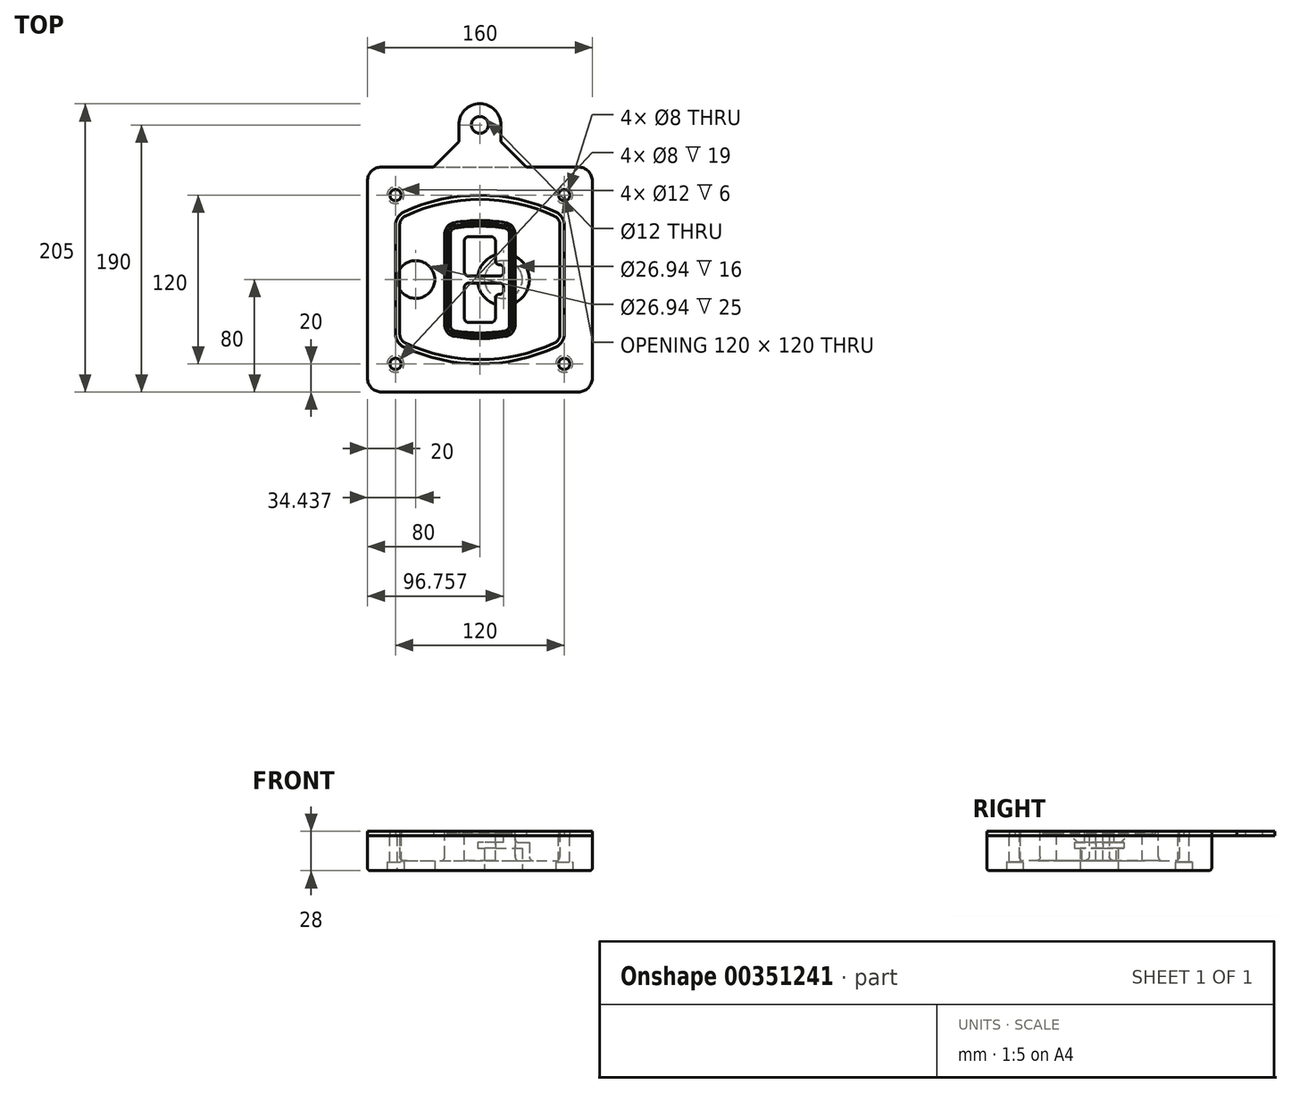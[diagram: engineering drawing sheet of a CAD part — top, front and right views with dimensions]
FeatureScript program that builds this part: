
annotation { "Feature Type Name" : "Feature", "Feature Type Description" : "" }
export const myFeature = defineFeature(function(context is Context, id is Id, definition is map)
    precondition{}
    {
        {
            var Q0;
            Q0=qCreatedBy(makeId("Top.planeOp"),FACE);
            var sketch = newSketch(context, id + "F0", { "sketchPlane" : qUnion([Q0])});
            skPoint(sketch, "E0.rect.middle", {"position": v(0, 0) * mm});
            skLineSegment(sketch, "E1.bottom", {"start": v(-70, -80) * mm, "end": v(70, -80) * mm});
            skLineSegment(sketch, "E1.top", {"start": v(-70, 80) * mm, "end": v(70, 80) * mm});
            skLineSegment(sketch, "E1.left", {"start": v(-80, -70) * mm, "end": v(-80, 70) * mm});
            skLineSegment(sketch, "E1.right", {"start": v(80, -70) * mm, "end": v(80, 70) * mm});
            skLineSegment(sketch, "E2", {"start": v(-80, 80) * mm, "end": v(80, -80) * mm, "construction": true});
            skLineSegment(sketch, "E3", {"start": v(80, 80) * mm, "end": v(-80, -80) * mm, "construction": true});
            skCircle(sketch, "E4", {"center": v(-60, 60) * mm, "radius": 4 * mm});
            skCircle(sketch, "E5", {"center": v(60, 60) * mm, "radius": 4 * mm});
            skCircle(sketch, "E6", {"center": v(60, -60) * mm, "radius": 4 * mm});
            skCircle(sketch, "E7", {"center": v(-60, -60) * mm, "radius": 4 * mm});
            skLineSegment(sketch, "E8", {"start": v(-60, 60) * mm, "end": v(60, 60) * mm, "construction": true});
            skLineSegment(sketch, "E9", {"start": v(60, 60) * mm, "end": v(60, -60) * mm, "construction": true});
            skLineSegment(sketch, "E10", {"start": v(60, -60) * mm, "end": v(-60, -60) * mm, "construction": true});
            skLineSegment(sketch, "E11", {"start": v(-60, -60) * mm, "end": v(-60, 60) * mm, "construction": true});
            skLineSegment(sketch, "E12", {"start": v(-60, 38.83) * mm, "end": v(-60, -38.83) * mm});
            skLineSegment(sketch, "E13", {"start": v(60, 38.83) * mm, "end": v(60, -38.83) * mm});
            skArc(sketch, "E14", {"start": v(54.26, 47.88) * mm, "mid": v(0, 60) * mm, "end": v(-54.26, 47.88) * mm});
            skArc(sketch, "E15", {"start": v(-54.26, -47.88) * mm, "mid": v(0, -60) * mm, "end": v(54.26, -47.88) * mm});
            skLineSegment(sketch, "E16", {"start": v(-60, 0) * mm, "end": v(60, 0) * mm, "construction": true});
            skPoint(sketch, "E17.visualSharp", {"position": v(-60, -45) * mm});
            skArc(sketch, "E17.filletArc", {"start": v(-60, -38.83) * mm, "mid": v(-58.44, -44.2) * mm, "end": v(-54.26, -47.88) * mm});
            skPoint(sketch, "E18.visualSharp", {"position": v(-60, 45) * mm});
            skArc(sketch, "E18.filletArc", {"start": v(-54.26, 47.88) * mm, "mid": v(-58.44, 44.2) * mm, "end": v(-60, 38.83) * mm});
            skPoint(sketch, "E19.visualSharp", {"position": v(60, 45) * mm});
            skArc(sketch, "E19.filletArc", {"start": v(60, 38.83) * mm, "mid": v(58.44, 44.2) * mm, "end": v(54.26, 47.88) * mm});
            skPoint(sketch, "E20.visualSharp", {"position": v(60, -45) * mm});
            skArc(sketch, "E20.filletArc", {"start": v(54.26, -47.88) * mm, "mid": v(58.44, -44.2) * mm, "end": v(60, -38.83) * mm});
            skPoint(sketch, "E21.visualSharp", {"position": v(-80, 80) * mm});
            skArc(sketch, "E21.filletArc", {"start": v(-70, 80) * mm, "mid": v(-77.07, 77.07) * mm, "end": v(-80, 70) * mm});
            skPoint(sketch, "E22.visualSharp", {"position": v(80, 80) * mm});
            skArc(sketch, "E22.filletArc", {"start": v(80, 70) * mm, "mid": v(77.07, 77.07) * mm, "end": v(70, 80) * mm});
            skPoint(sketch, "E23.visualSharp", {"position": v(80, -80) * mm});
            skArc(sketch, "E23.filletArc", {"start": v(70, -80) * mm, "mid": v(77.07, -77.07) * mm, "end": v(80, -70) * mm});
            skPoint(sketch, "E24.visualSharp", {"position": v(-80, -80) * mm});
            skArc(sketch, "E24.filletArc", {"start": v(-80, -70) * mm, "mid": v(-77.07, -77.07) * mm, "end": v(-70, -80) * mm});
            skArc(sketch, "E25.0", {"start": v(57, 38.83) * mm, "mid": v(55.9, 42.58) * mm, "end": v(52.98, 45.17) * mm});
            skLineSegment(sketch, "E25.1", {"start": v(57, 38.83) * mm, "end": v(57, -38.83) * mm});
            skArc(sketch, "E25.2", {"start": v(52.98, -45.17) * mm, "mid": v(55.9, -42.58) * mm, "end": v(57, -38.83) * mm});
            skArc(sketch, "E25.3", {"start": v(-52.98, -45.17) * mm, "mid": v(0, -57) * mm, "end": v(52.98, -45.17) * mm});
            skArc(sketch, "E25.4", {"start": v(-57, -38.83) * mm, "mid": v(-55.9, -42.58) * mm, "end": v(-52.98, -45.17) * mm});
            skArc(sketch, "E25.5", {"start": v(52.98, 45.17) * mm, "mid": v(0, 57) * mm, "end": v(-52.98, 45.17) * mm});
            skLineSegment(sketch, "E25.6", {"start": v(-57, 38.83) * mm, "end": v(-57, -38.83) * mm});
            skArc(sketch, "E25.7", {"start": v(-52.98, 45.17) * mm, "mid": v(-55.9, 42.58) * mm, "end": v(-57, 38.83) * mm});
            skArc(sketch, "E26.0", {"start": v(-55.96, 51.5) * mm, "mid": v(-61.82, 46.33) * mm, "end": v(-64, 38.83) * mm});
            skArc(sketch, "E26.1", {"start": v(55.96, 51.5) * mm, "mid": v(0, 64) * mm, "end": v(-55.96, 51.5) * mm});
            skArc(sketch, "E26.2", {"start": v(64, 38.83) * mm, "mid": v(61.82, 46.33) * mm, "end": v(55.96, 51.5) * mm});
            skLineSegment(sketch, "E26.3", {"start": v(64, 38.83) * mm, "end": v(64, -38.83) * mm});
            skArc(sketch, "E26.4", {"start": v(55.96, -51.5) * mm, "mid": v(61.82, -46.33) * mm, "end": v(64, -38.83) * mm});
            skLineSegment(sketch, "E26.5", {"start": v(-64, 38.83) * mm, "end": v(-64, -38.83) * mm});
            skArc(sketch, "E26.6", {"start": v(-55.96, -51.5) * mm, "mid": v(0, -64) * mm, "end": v(55.96, -51.5) * mm});
            skArc(sketch, "E26.7", {"start": v(-64, -38.83) * mm, "mid": v(-61.82, -46.33) * mm, "end": v(-55.96, -51.5) * mm});
            skSolve(sketch);
        }
        {
            var Q0;
            Q0=makeQuery(id+"F0.imprint","IMPRINT",FACE,{"disambiguationData":[TD([[makeQuery(id+"F0.imprint","IMPRINT",EDGE,{"derivedFrom":sQuery(id+"F0.wireOp",EDGE,"E1.bottom")}),1.0]])]});
            var Q1;
            Q1=makeQuery(id+"F0.imprint","IMPRINT",FACE,{"disambiguationData":[TD([[makeQuery(id+"F0.imprint","IMPRINT",EDGE,{"derivedFrom":sQuery(id+"F0.wireOp",EDGE,"E12")}),1.0]])]});
            var Q2;
            Q2=makeQuery(id+"F0.imprint","IMPRINT",FACE,{"disambiguationData":[TD([[makeQuery(id+"F0.imprint","IMPRINT",EDGE,{"derivedFrom":sQuery(id+"F0.wireOp",EDGE,"E25.0")}),1.0]])]});
            var Q3;
            Q3=makeQuery(id+"F0.imprint","IMPRINT",FACE,{"disambiguationData":[TD([[makeQuery(id+"F0.imprint","IMPRINT",EDGE,{"derivedFrom":sQuery(id+"F0.wireOp",EDGE,"E12")}),-1.0]])]});
            extrude(context, id + "F1", {"entities" : qUnion([Q0, Q1, Q2, Q3]), "oppositeDirection" : true, "depth" : 25 * mm});
        }
        {
            var Q0;
            Q0=makeQuery(id+"F0.imprint","IMPRINT",FACE,{"disambiguationData":[TD([[makeQuery(id+"F0.imprint","IMPRINT",EDGE,{"derivedFrom":sQuery(id+"F0.wireOp",EDGE,"E12")}),1.0]])]});
            extrude(context, id + "F2", {"entities" : qUnion([Q0]), "operationType" : NewBodyOperationType.ADD, "depth" : 3 * mm});
        }
        {
            var Q0;
            Q0=makeQuery(id+"F0.imprint","IMPRINT",FACE,{"disambiguationData":[TD([[makeQuery(id+"F0.imprint","IMPRINT",EDGE,{"derivedFrom":sQuery(id+"F0.wireOp",EDGE,"E25.0")}),1.0]])]});
            extrude(context, id + "F3", {"entities" : qUnion([Q0]), "operationType" : NewBodyOperationType.REMOVE, "oppositeDirection" : true, "depth" : 18 * mm});
        }
        {
            var Q0;
            Q0=makeQuery(id+"F2.opExtrude","CAP_FACE",FACE,{"disambiguationData":[OSD([sQuery(id+"F0.wireOp",EDGE,"E12"),sQuery(id+"F0.wireOp",EDGE,"E13"),sQuery(id+"F0.wireOp",EDGE,"E14"),sQuery(id+"F0.wireOp",EDGE,"E15"),sQuery(id+"F0.wireOp",EDGE,"E17.filletArc"),sQuery(id+"F0.wireOp",EDGE,"E18.filletArc"),sQuery(id+"F0.wireOp",EDGE,"E19.filletArc"),sQuery(id+"F0.wireOp",EDGE,"E20.filletArc"),sQuery(id+"F0.wireOp",EDGE,"E25.0"),sQuery(id+"F0.wireOp",EDGE,"E25.1"),sQuery(id+"F0.wireOp",EDGE,"E25.2"),sQuery(id+"F0.wireOp",EDGE,"E25.3"),sQuery(id+"F0.wireOp",EDGE,"E25.4"),sQuery(id+"F0.wireOp",EDGE,"E25.5"),sQuery(id+"F0.wireOp",EDGE,"E25.6"),sQuery(id+"F0.wireOp",EDGE,"E25.7")])],"isStart":false});
            var sketch = newSketch(context, id + "F4", { "sketchPlane" : qUnion([Q0])});
            skArc(sketch, "E27.0", {"start": v(-18.34, -40.45) * mm, "mid": v(0, -42) * mm, "end": v(18.34, -40.45) * mm});
            skArc(sketch, "E28.0", {"start": v(18.34, 40.45) * mm, "mid": v(0, 42) * mm, "end": v(-18.34, 40.45) * mm});
            skLineSegment(sketch, "E29", {"start": v(-25, 32.57) * mm, "end": v(-25, -32.57) * mm});
            skLineSegment(sketch, "E30", {"start": v(25, 32.57) * mm, "end": v(25, -32.57) * mm});
            skLineSegment(sketch, "E31", {"start": v(-25, 39.1) * mm, "end": v(25, 39.1) * mm, "construction": true});
            skLineSegment(sketch, "E32", {"start": v(-25, -39.1) * mm, "end": v(25, -39.1) * mm, "construction": true});
            skPoint(sketch, "E33.visualSharp", {"position": v(-25, 39.1) * mm});
            skArc(sketch, "E33.filletArc", {"start": v(-18.34, 40.45) * mm, "mid": v(-23.11, 37.73) * mm, "end": v(-25, 32.57) * mm});
            skPoint(sketch, "E34.visualSharp", {"position": v(25, 39.1) * mm});
            skArc(sketch, "E34.filletArc", {"start": v(25, 32.57) * mm, "mid": v(23.11, 37.73) * mm, "end": v(18.34, 40.45) * mm});
            skPoint(sketch, "E35.visualSharp", {"position": v(25, -39.1) * mm});
            skArc(sketch, "E35.filletArc", {"start": v(18.34, -40.45) * mm, "mid": v(23.11, -37.73) * mm, "end": v(25, -32.57) * mm});
            skPoint(sketch, "E36.visualSharp", {"position": v(-25, -39.1) * mm});
            skArc(sketch, "E36.filletArc", {"start": v(-25, -32.57) * mm, "mid": v(-23.11, -37.73) * mm, "end": v(-18.34, -40.45) * mm});
            skArc(sketch, "E37.0", {"start": v(52.98, 45.17) * mm, "mid": v(0, 57) * mm, "end": v(-52.98, 45.17) * mm});
            skArc(sketch, "E37.1", {"start": v(-52.98, 45.17) * mm, "mid": v(-55.9, 42.58) * mm, "end": v(-57, 38.83) * mm});
            skLineSegment(sketch, "E37.2", {"start": v(-57, 38.83) * mm, "end": v(-57, -38.83) * mm});
            skArc(sketch, "E37.3", {"start": v(-57, -38.83) * mm, "mid": v(-55.9, -42.58) * mm, "end": v(-52.98, -45.17) * mm});
            skArc(sketch, "E37.4", {"start": v(-52.98, -45.17) * mm, "mid": v(0, -57) * mm, "end": v(52.98, -45.17) * mm});
            skArc(sketch, "E37.5", {"start": v(52.98, -45.17) * mm, "mid": v(55.9, -42.58) * mm, "end": v(57, -38.83) * mm});
            skLineSegment(sketch, "E37.6", {"start": v(57, 38.83) * mm, "end": v(57, -38.83) * mm});
            skArc(sketch, "E37.7", {"start": v(57, 38.83) * mm, "mid": v(55.9, 42.58) * mm, "end": v(52.98, 45.17) * mm});
            skLineSegment(sketch, "E38.0", {"start": v(23, 32.57) * mm, "end": v(23, -32.57) * mm});
            skArc(sketch, "E38.1", {"start": v(18, -38.48) * mm, "mid": v(21.58, -36.44) * mm, "end": v(23, -32.57) * mm});
            skArc(sketch, "E38.2", {"start": v(-18, -38.48) * mm, "mid": v(0, -40) * mm, "end": v(18, -38.48) * mm});
            skArc(sketch, "E38.3", {"start": v(-23, -32.57) * mm, "mid": v(-21.58, -36.44) * mm, "end": v(-18, -38.48) * mm});
            skLineSegment(sketch, "E38.4", {"start": v(-23, 32.57) * mm, "end": v(-23, -32.57) * mm});
            skArc(sketch, "E38.5", {"start": v(23, 32.57) * mm, "mid": v(21.58, 36.44) * mm, "end": v(18, 38.48) * mm});
            skArc(sketch, "E38.6", {"start": v(-18, 38.48) * mm, "mid": v(-21.58, 36.44) * mm, "end": v(-23, 32.57) * mm});
            skArc(sketch, "E38.7", {"start": v(18, 38.48) * mm, "mid": v(0, 40) * mm, "end": v(-18, 38.48) * mm});
            skArc(sketch, "E39.0", {"start": v(21, 32.57) * mm, "mid": v(20.06, 35.15) * mm, "end": v(17.67, 36.5) * mm});
            skLineSegment(sketch, "E39.1", {"start": v(21, 32.57) * mm, "end": v(21, -32.57) * mm});
            skArc(sketch, "E39.2", {"start": v(17.67, -36.5) * mm, "mid": v(20.06, -35.15) * mm, "end": v(21, -32.57) * mm});
            skArc(sketch, "E39.3", {"start": v(-17.67, -36.5) * mm, "mid": v(0, -38) * mm, "end": v(17.67, -36.5) * mm});
            skArc(sketch, "E39.4", {"start": v(-21, -32.57) * mm, "mid": v(-20.06, -35.15) * mm, "end": v(-17.67, -36.5) * mm});
            skArc(sketch, "E39.5", {"start": v(17.67, 36.5) * mm, "mid": v(0, 38) * mm, "end": v(-17.67, 36.5) * mm});
            skLineSegment(sketch, "E39.6", {"start": v(-21, 32.57) * mm, "end": v(-21, -32.57) * mm});
            skArc(sketch, "E39.7", {"start": v(-17.67, 36.5) * mm, "mid": v(-20.06, 35.15) * mm, "end": v(-21, 32.57) * mm});
            skLineSegment(sketch, "E40", {"start": v(-25, 0) * mm, "end": v(25, 0) * mm, "construction": true});
            skLineSegment(sketch, "E41", {"start": v(-11, 5.5) * mm, "end": v(-11, 27.5) * mm});
            skLineSegment(sketch, "E42", {"start": v(-8, 30.5) * mm, "end": v(8, 30.5) * mm});
            skLineSegment(sketch, "E43", {"start": v(11, 27.5) * mm, "end": v(11, 13.5) * mm});
            skLineSegment(sketch, "E44", {"start": v(14, 10.5) * mm, "end": v(14, 10.5) * mm});
            skLineSegment(sketch, "E45", {"start": v(17, 7.5) * mm, "end": v(17, 5.5) * mm});
            skLineSegment(sketch, "E46", {"start": v(14, 2.5) * mm, "end": v(-8, 2.5) * mm});
            skPoint(sketch, "E47.visualSharp", {"position": v(-11, 30.5) * mm});
            skArc(sketch, "E47.filletArc", {"start": v(-8, 30.5) * mm, "mid": v(-10.12, 29.62) * mm, "end": v(-11, 27.5) * mm});
            skPoint(sketch, "E48.visualSharp", {"position": v(11, 30.5) * mm});
            skArc(sketch, "E48.filletArc", {"start": v(11, 27.5) * mm, "mid": v(10.12, 29.62) * mm, "end": v(8, 30.5) * mm});
            skPoint(sketch, "E49.visualSharp", {"position": v(11, 10.5) * mm});
            skArc(sketch, "E49.filletArc", {"start": v(11, 13.5) * mm, "mid": v(11.88, 11.38) * mm, "end": v(14, 10.5) * mm});
            skPoint(sketch, "E50.visualSharp", {"position": v(17, 10.5) * mm});
            skArc(sketch, "E50.filletArc", {"start": v(17, 7.5) * mm, "mid": v(16.12, 9.62) * mm, "end": v(14, 10.5) * mm});
            skPoint(sketch, "E51.visualSharp", {"position": v(17, 2.5) * mm});
            skArc(sketch, "E51.filletArc", {"start": v(14, 2.5) * mm, "mid": v(16.12, 3.38) * mm, "end": v(17, 5.5) * mm});
            skPoint(sketch, "E52.visualSharp", {"position": v(-11, 2.5) * mm});
            skArc(sketch, "E52.filletArc", {"start": v(-11, 5.5) * mm, "mid": v(-10.12, 3.38) * mm, "end": v(-8, 2.5) * mm});
            skLineSegment(sketch, "E53.0.MirrorCS", {"start": v(14, -2.5) * mm, "end": v(-8, -2.5) * mm});
            skArc(sketch, "E54.0.MirrorCS", {"start": v(-11, -5.5) * mm, "mid": v(-10.12, -3.38) * mm, "end": v(-8, -2.5) * mm});
            skLineSegment(sketch, "E55.0.MirrorCS", {"start": v(-11, -5.5) * mm, "end": v(-11, -27.5) * mm});
            skArc(sketch, "E56.0.MirrorCS", {"start": v(-8, -30.5) * mm, "mid": v(-10.12, -29.62) * mm, "end": v(-11, -27.5) * mm});
            skLineSegment(sketch, "E57.0.MirrorCS", {"start": v(-8, -30.5) * mm, "end": v(8, -30.5) * mm});
            skArc(sketch, "E58.0.MirrorCS", {"start": v(11, -27.5) * mm, "mid": v(10.12, -29.62) * mm, "end": v(8, -30.5) * mm});
            skLineSegment(sketch, "E59.0.MirrorCS", {"start": v(11, -27.5) * mm, "end": v(11, -13.5) * mm});
            skArc(sketch, "E60.0.MirrorCS", {"start": v(11, -13.5) * mm, "mid": v(11.88, -11.38) * mm, "end": v(14, -10.5) * mm});
            skArc(sketch, "E61.0.MirrorCS", {"start": v(17, -7.5) * mm, "mid": v(16.12, -9.62) * mm, "end": v(14, -10.5) * mm});
            skLineSegment(sketch, "E62.0.MirrorCS", {"start": v(17, -7.5) * mm, "end": v(17, -5.5) * mm});
            skArc(sketch, "E63.0.MirrorCS", {"start": v(14, -2.5) * mm, "mid": v(16.12, -3.38) * mm, "end": v(17, -5.5) * mm});
            skSolve(sketch);
        }
        {
            var Q0;
            Q0=makeQuery(id+"F4.imprint","IMPRINT",FACE,{"disambiguationData":[TD([[makeQuery(id+"F4.imprint","IMPRINT",EDGE,{"derivedFrom":sQuery(id+"F4.wireOp",EDGE,"E27.0")}),1.0]])]});
            var Q1;
            Q1=makeQuery(id+"F4.imprint","IMPRINT",FACE,{"disambiguationData":[TD([[makeQuery(id+"F4.imprint","IMPRINT",EDGE,{"derivedFrom":sQuery(id+"F4.wireOp",EDGE,"E38.0")}),-1.0]])]});
            var Q2;
            Q2=makeQuery(id+"F4.imprint","IMPRINT",FACE,{"disambiguationData":[TD([[makeQuery(id+"F4.imprint","IMPRINT",EDGE,{"derivedFrom":sQuery(id+"F4.wireOp",EDGE,"E39.0")}),1.0]])]});
            extrude(context, id + "F5", {"entities" : qUnion([Q0, Q1, Q2]), "operationType" : NewBodyOperationType.ADD, "endBound" : BoundingType.UP_TO_NEXT, "oppositeDirection" : true, "depth" : 25 * mm});
        }
        {
            var Q0;
            Q0=makeQuery(id+"F4.imprint","IMPRINT",FACE,{"disambiguationData":[TD([[makeQuery(id+"F4.imprint","IMPRINT",EDGE,{"derivedFrom":sQuery(id+"F4.wireOp",EDGE,"E38.0")}),-1.0]])]});
            extrude(context, id + "F6", {"entities" : qUnion([Q0]), "operationType" : NewBodyOperationType.REMOVE, "oppositeDirection" : true, "depth" : 2 * mm});
        }
        {
            var Q0;
            Q0=makeQuery(id+"F1.opExtrude","CAP_FACE",FACE,{"disambiguationData":[OSD([sQuery(id+"F0.wireOp",EDGE,"E1.bottom"),sQuery(id+"F0.wireOp",EDGE,"E1.top"),sQuery(id+"F0.wireOp",EDGE,"E1.left"),sQuery(id+"F0.wireOp",EDGE,"E1.right"),sQuery(id+"F0.wireOp",EDGE,"E4"),sQuery(id+"F0.wireOp",EDGE,"E5"),sQuery(id+"F0.wireOp",EDGE,"E6"),sQuery(id+"F0.wireOp",EDGE,"E7"),sQuery(id+"F0.wireOp",EDGE,"E21.filletArc"),sQuery(id+"F0.wireOp",EDGE,"E22.filletArc"),sQuery(id+"F0.wireOp",EDGE,"E23.filletArc"),sQuery(id+"F0.wireOp",EDGE,"E24.filletArc")])],"isStart":false});
            var sketch = newSketch(context, id + "F7", { "sketchPlane" : qUnion([Q0])});
            skCircle(sketch, "E64", {"center": v(16.76, 0) * mm, "radius": 13.47 * mm});
            skCircle(sketch, "E65", {"center": v(-45.56, 0) * mm, "radius": 13.47 * mm});
            skLineSegment(sketch, "E66", {"start": v(80, 0) * mm, "end": v(-80, 0) * mm});
            skCircle(sketch, "E67", {"center": v(16.76, 0) * mm, "radius": 18.47 * mm});
            skCircle(sketch, "E68", {"center": v(60, -60) * mm, "radius": 6 * mm});
            skCircle(sketch, "E69", {"center": v(-60, -60) * mm, "radius": 6 * mm});
            skCircle(sketch, "E70", {"center": v(-60, 60) * mm, "radius": 6 * mm});
            skCircle(sketch, "E71", {"center": v(60, 60) * mm, "radius": 6 * mm});
            skSolve(sketch);
        }
        {
            var Q0;
            {var subQ1=sQuery(id+"F7.wireOp",EDGE,"E66");var subQ4=sQuery(id+"F7.wireOp",EDGE,"E64");var subQ6=makeQuery(id+"F7.imprint","INTERSECT",VERTEX,{"disambiguationData":[OD(0.0)],"derivedFrom":[subQ4,subQ1]});Q0=makeQuery(id+"F7.imprint","IMPRINT",FACE,{"disambiguationData":[TD([[makeQuery(id+"F7.imprint","IMPRINT",EDGE,{"disambiguationData":[TD([[subQ6,-1.0]])],"derivedFrom":subQ4}),-1.0]])]});}
            var Q1;
            {var subQ0=sQuery(id+"F7.wireOp",EDGE,"E66");var subQ1=sQuery(id+"F7.wireOp",EDGE,"E64");var subQ3=makeQuery(id+"F7.imprint","INTERSECT",VERTEX,{"disambiguationData":[OD(0.0)],"derivedFrom":[subQ1,subQ0]});Q1=makeQuery(id+"F7.imprint","IMPRINT",FACE,{"disambiguationData":[TD([[makeQuery(id+"F7.imprint","IMPRINT",EDGE,{"disambiguationData":[TD([[subQ3,-1.0]])],"derivedFrom":subQ1}),1.0]])]});}
            var Q2;
            {var subQ0=sQuery(id+"F7.wireOp",EDGE,"E66");var subQ1=sQuery(id+"F7.wireOp",EDGE,"E64");var subQ3=makeQuery(id+"F7.imprint","INTERSECT",VERTEX,{"disambiguationData":[OD(0.0)],"derivedFrom":[subQ1,subQ0]});Q2=makeQuery(id+"F7.imprint","IMPRINT",FACE,{"disambiguationData":[TD([[makeQuery(id+"F7.imprint","IMPRINT",EDGE,{"disambiguationData":[TD([[subQ3,1.0]])],"derivedFrom":subQ1}),1.0]])]});}
            var Q3;
            {var subQ1=sQuery(id+"F7.wireOp",EDGE,"E66");var subQ4=sQuery(id+"F7.wireOp",EDGE,"E64");var subQ6=makeQuery(id+"F7.imprint","INTERSECT",VERTEX,{"disambiguationData":[OD(0.0)],"derivedFrom":[subQ4,subQ1]});Q3=makeQuery(id+"F7.imprint","IMPRINT",FACE,{"disambiguationData":[TD([[makeQuery(id+"F7.imprint","IMPRINT",EDGE,{"disambiguationData":[TD([[subQ6,1.0]])],"derivedFrom":subQ4}),-1.0]])]});}
            extrude(context, id + "F8", {"entities" : qUnion([Q0, Q1, Q2, Q3]), "operationType" : NewBodyOperationType.ADD, "oppositeDirection" : true, "depth" : 20 * mm});
        }
        {
            var Q0;
            {var subQ0=sQuery(id+"F7.wireOp",EDGE,"E66");var subQ1=sQuery(id+"F7.wireOp",EDGE,"E64");var subQ3=makeQuery(id+"F7.imprint","INTERSECT",VERTEX,{"disambiguationData":[OD(0.0)],"derivedFrom":[subQ1,subQ0]});Q0=makeQuery(id+"F7.imprint","IMPRINT",FACE,{"disambiguationData":[TD([[makeQuery(id+"F7.imprint","IMPRINT",EDGE,{"disambiguationData":[TD([[subQ3,-1.0]])],"derivedFrom":subQ1}),1.0]])]});}
            var Q1;
            {var subQ0=sQuery(id+"F7.wireOp",EDGE,"E66");var subQ1=sQuery(id+"F7.wireOp",EDGE,"E64");var subQ3=makeQuery(id+"F7.imprint","INTERSECT",VERTEX,{"disambiguationData":[OD(0.0)],"derivedFrom":[subQ1,subQ0]});Q1=makeQuery(id+"F7.imprint","IMPRINT",FACE,{"disambiguationData":[TD([[makeQuery(id+"F7.imprint","IMPRINT",EDGE,{"disambiguationData":[TD([[subQ3,1.0]])],"derivedFrom":subQ1}),1.0]])]});}
            extrude(context, id + "F9", {"entities" : qUnion([Q0, Q1]), "operationType" : NewBodyOperationType.REMOVE, "oppositeDirection" : true, "depth" : 16 * mm});
        }
        {
            var Q0;
            {var subQ0=sQuery(id+"F7.wireOp",EDGE,"E66");var subQ1=sQuery(id+"F7.wireOp",EDGE,"E65");var subQ3=makeQuery(id+"F7.imprint","INTERSECT",VERTEX,{"disambiguationData":[OD(0.0)],"derivedFrom":[subQ1,subQ0]});Q0=makeQuery(id+"F7.imprint","IMPRINT",FACE,{"disambiguationData":[TD([[makeQuery(id+"F7.imprint","IMPRINT",EDGE,{"disambiguationData":[TD([[subQ3,-1.0]])],"derivedFrom":subQ1}),1.0]])]});}
            var Q1;
            {var subQ0=sQuery(id+"F7.wireOp",EDGE,"E66");var subQ1=sQuery(id+"F7.wireOp",EDGE,"E65");var subQ3=makeQuery(id+"F7.imprint","INTERSECT",VERTEX,{"disambiguationData":[OD(0.0)],"derivedFrom":[subQ1,subQ0]});Q1=makeQuery(id+"F7.imprint","IMPRINT",FACE,{"disambiguationData":[TD([[makeQuery(id+"F7.imprint","IMPRINT",EDGE,{"disambiguationData":[TD([[subQ3,1.0]])],"derivedFrom":subQ1}),1.0]])]});}
            extrude(context, id + "F10", {"entities" : qUnion([Q0, Q1]), "operationType" : NewBodyOperationType.REMOVE, "oppositeDirection" : true, "depth" : 25 * mm});
        }
        {
            var Q0;
            Q0=makeQuery(id+"F7.imprint","IMPRINT",FACE,{"disambiguationData":[TD([[makeQuery(id+"F7.imprint","IMPRINT",EDGE,{"derivedFrom":sQuery(id+"F7.wireOp",EDGE,"E68")}),1.0]])]});
            var Q1;
            Q1=makeQuery(id+"F7.imprint","IMPRINT",FACE,{"disambiguationData":[TD([[makeQuery(id+"F7.imprint","IMPRINT",EDGE,{"derivedFrom":makeQuery(id+"F1.opExtrude","CAP_EDGE",EDGE,{"disambiguationData":[OSD([sQuery(id+"F0.wireOp",EDGE,"E5")])],"isStart":false})}),-1.0]])]});
            var Q2;
            Q2=makeQuery(id+"F7.imprint","IMPRINT",FACE,{"disambiguationData":[TD([[makeQuery(id+"F7.imprint","IMPRINT",EDGE,{"derivedFrom":sQuery(id+"F7.wireOp",EDGE,"E69")}),1.0]])]});
            var Q3;
            Q3=makeQuery(id+"F7.imprint","IMPRINT",FACE,{"disambiguationData":[TD([[makeQuery(id+"F7.imprint","IMPRINT",EDGE,{"derivedFrom":makeQuery(id+"F1.opExtrude","CAP_EDGE",EDGE,{"disambiguationData":[OSD([sQuery(id+"F0.wireOp",EDGE,"E4")])],"isStart":false})}),-1.0]])]});
            var Q4;
            Q4=makeQuery(id+"F7.imprint","IMPRINT",FACE,{"disambiguationData":[TD([[makeQuery(id+"F7.imprint","IMPRINT",EDGE,{"derivedFrom":sQuery(id+"F7.wireOp",EDGE,"E70")}),1.0]])]});
            var Q5;
            Q5=makeQuery(id+"F7.imprint","IMPRINT",FACE,{"disambiguationData":[TD([[makeQuery(id+"F7.imprint","IMPRINT",EDGE,{"derivedFrom":makeQuery(id+"F1.opExtrude","CAP_EDGE",EDGE,{"disambiguationData":[OSD([sQuery(id+"F0.wireOp",EDGE,"E7")])],"isStart":false})}),-1.0]])]});
            var Q6;
            Q6=makeQuery(id+"F7.imprint","IMPRINT",FACE,{"disambiguationData":[TD([[makeQuery(id+"F7.imprint","IMPRINT",EDGE,{"derivedFrom":sQuery(id+"F7.wireOp",EDGE,"E71")}),1.0]])]});
            var Q7;
            Q7=makeQuery(id+"F7.imprint","IMPRINT",FACE,{"disambiguationData":[TD([[makeQuery(id+"F7.imprint","IMPRINT",EDGE,{"derivedFrom":makeQuery(id+"F1.opExtrude","CAP_EDGE",EDGE,{"disambiguationData":[OSD([sQuery(id+"F0.wireOp",EDGE,"E6")])],"isStart":false})}),-1.0]])]});
            extrude(context, id + "F11", {"entities" : qUnion([Q0, Q1, Q2, Q3, Q4, Q5, Q6, Q7]), "operationType" : NewBodyOperationType.REMOVE, "oppositeDirection" : true, "depth" : 6 * mm});
        }
        {
            var Q0;
            Q0=makeQuery(id+"F9.boolean.opBoolean","COPY",FACE,{"derivedFrom":makeQuery(id+"F9.opExtrude","CAP_FACE",FACE,{"disambiguationData":[OSD([sQuery(id+"F7.wireOp",EDGE,"E64")])],"isStart":false})});
            var sketch = newSketch(context, id + "F12", { "sketchPlane" : qUnion([Q0])});
            skArc(sketch, "E72.0", {"start": v(11, 17.55) * mm, "mid": v(2.57, 11.82) * mm, "end": v(-1.54, 2.5) * mm});
            skArc(sketch, "E72.1", {"start": v(-1.54, -2.5) * mm, "mid": v(2.57, -11.82) * mm, "end": v(11, -17.55) * mm});
            skLineSegment(sketch, "E73", {"start": v(-1.54, -2.5) * mm, "end": v(14, -2.5) * mm});
            skLineSegment(sketch, "E74.0", {"start": v(14, 2.5) * mm, "end": v(-1.54, 2.5) * mm});
            skArc(sketch, "E74.1", {"start": v(14, 2.5) * mm, "mid": v(16.12, 3.38) * mm, "end": v(17, 5.5) * mm});
            skLineSegment(sketch, "E74.2", {"start": v(17, 7.5) * mm, "end": v(17, 5.5) * mm});
            skArc(sketch, "E74.3", {"start": v(17, 7.5) * mm, "mid": v(16.12, 9.62) * mm, "end": v(14, 10.5) * mm});
            skArc(sketch, "E74.4", {"start": v(11, 13.5) * mm, "mid": v(11.88, 11.38) * mm, "end": v(14, 10.5) * mm});
            skLineSegment(sketch, "E74.5", {"start": v(11, 17.55) * mm, "end": v(11, 13.5) * mm});
            skLineSegment(sketch, "E74.7", {"start": v(14, -2.5) * mm, "end": v(-1.54, -2.5) * mm});
            skArc(sketch, "E74.8", {"start": v(14, -2.5) * mm, "mid": v(16.12, -3.38) * mm, "end": v(17, -5.5) * mm});
            skLineSegment(sketch, "E74.9", {"start": v(17, -7.5) * mm, "end": v(17, -5.5) * mm});
            skArc(sketch, "E74.10", {"start": v(17, -7.5) * mm, "mid": v(16.12, -9.62) * mm, "end": v(14, -10.5) * mm});
            skArc(sketch, "E74.11", {"start": v(11, -13.5) * mm, "mid": v(11.88, -11.38) * mm, "end": v(14, -10.5) * mm});
            skLineSegment(sketch, "E74.12", {"start": v(11, -17.55) * mm, "end": v(11, -13.5) * mm});
            skPoint(sketch, "E75.orphan", {"position": v(11, -27.5) * mm});
            skPoint(sketch, "E76.orphan", {"position": v(-8, -2.5) * mm});
            skPoint(sketch, "E77.orphan", {"position": v(-8, 2.5) * mm});
            skPoint(sketch, "E78.orphan", {"position": v(11, 27.5) * mm});
            skSolve(sketch);
        }
        {
            var Q0;
            {var subQ7=sQuery(id+"F12.wireOp",EDGE,"E72.0");var subQ14=sQuery(id+"F12.wireOp",EDGE,"E72.1");var subQ16=sQuery(id+"F12.wireOp",EDGE,"E74.1");var subQ18=sQuery(id+"F12.wireOp",EDGE,"E74.8");Q0=qUnion([makeQuery(id+"F12.imprint","IMPRINT",FACE,{"disambiguationData":[TD([[makeQuery(id+"F12.imprint","IMPRINT",EDGE,{"derivedFrom":subQ7}),1.0]])]}),makeQuery(id+"F12.imprint","IMPRINT",FACE,{"disambiguationData":[TD([[makeQuery(id+"F12.imprint","IMPRINT",EDGE,{"derivedFrom":subQ14}),1.0]])]}),makeQuery(id+"F12.imprint","IMPRINT",FACE,{"disambiguationData":[TD([[makeQuery(id+"F12.imprint","IMPRINT",EDGE,{"derivedFrom":subQ16}),1.0]])]}),makeQuery(id+"F12.imprint","IMPRINT",FACE,{"disambiguationData":[TD([[makeQuery(id+"F12.imprint","IMPRINT",EDGE,{"derivedFrom":subQ18}),-1.0]])]})]);}
            var Q1;
            Q1=makeQuery(id+"F5.boolean.opBoolean","SPLIT",FACE,{"disambiguationData":[TD([makeQuery(id+"F5.opExtrude","SWEPT_FACE",FACE,{"disambiguationData":[OSD([sQuery(id+"F4.wireOp",EDGE,"E41")])]})])],"derivedFrom":makeQuery(id+"F3.boolean.opBoolean","COPY",FACE,{"derivedFrom":makeQuery(id+"F3.opExtrude","CAP_FACE",FACE,{"disambiguationData":[OSD([sQuery(id+"F0.wireOp",EDGE,"E25.0"),sQuery(id+"F0.wireOp",EDGE,"E25.1"),sQuery(id+"F0.wireOp",EDGE,"E25.2"),sQuery(id+"F0.wireOp",EDGE,"E25.3"),sQuery(id+"F0.wireOp",EDGE,"E25.4"),sQuery(id+"F0.wireOp",EDGE,"E25.5"),sQuery(id+"F0.wireOp",EDGE,"E25.6"),sQuery(id+"F0.wireOp",EDGE,"E25.7")])],"isStart":false})})});
            extrude(context, id + "F13", {"entities" : qUnion([Q0]), "operationType" : NewBodyOperationType.REMOVE, "endBound" : BoundingType.UP_TO_SURFACE, "endBoundEntityFace" : qUnion([Q1]), "depth" : 25 * mm});
        }
        {
            var Q0;
            Q0=makeQuery(id+"F3.boolean.opBoolean","COPY",EDGE,{"derivedFrom":makeQuery(id+"F3.opExtrude","CAP_EDGE",EDGE,{"disambiguationData":[OSD([sQuery(id+"F0.wireOp",EDGE,"E25.6")])],"isStart":false})});
            var Q1;
            Q1=makeQuery(id+"F8.boolean.opBoolean","INTERSECT",EDGE,{"derivedFrom":[makeQuery(id+"F5.opExtrude","SWEPT_FACE",FACE,{"disambiguationData":[OSD([sQuery(id+"F4.wireOp",EDGE,"E30")])]}),makeQuery(id+"F8.opExtrude","CAP_FACE",FACE,{"disambiguationData":[OSD([sQuery(id+"F7.wireOp",EDGE,"E67")])],"isStart":false})]});
            var Q2;
            Q2=makeQuery(id+"F8.boolean.opBoolean","INTERSECT",EDGE,{"disambiguationData":[OD(1.0)],"derivedFrom":[makeQuery(id+"F5.opExtrude","SWEPT_FACE",FACE,{"disambiguationData":[OSD([sQuery(id+"F4.wireOp",EDGE,"E30")])]}),makeQuery(id+"F8.opExtrude","SWEPT_FACE",FACE,{"disambiguationData":[OSD([sQuery(id+"F7.wireOp",EDGE,"E67")])]})]});
            var Q3;
            {var subQ0=sQuery(id+"F4.wireOp",EDGE,"E30");Q3=makeQuery(id+"F8.boolean.opBoolean","SPLIT",EDGE,{"disambiguationData":[TD([makeQuery(id+"F5.opExtrude","SWEPT_FACE",FACE,{"disambiguationData":[OSD([sQuery(id+"F4.wireOp",EDGE,"E35.filletArc")])]})])],"derivedFrom":makeQuery(id+"F5.opExtrude","CAP_EDGE",EDGE,{"disambiguationData":[OSD([subQ0])],"isStart":false})});}
            var Q4;
            {var subQ0=sQuery(id+"F0.wireOp",EDGE,"E25.7");var subQ1=sQuery(id+"F0.wireOp",EDGE,"E25.1");var subQ2=sQuery(id+"F0.wireOp",EDGE,"E25.6");var subQ3=sQuery(id+"F0.wireOp",EDGE,"E25.5");var subQ4=sQuery(id+"F0.wireOp",EDGE,"E25.4");var subQ5=sQuery(id+"F0.wireOp",EDGE,"E25.0");var subQ6=sQuery(id+"F0.wireOp",EDGE,"E25.2");var subQ7=sQuery(id+"F0.wireOp",EDGE,"E25.3");Q4=makeQuery(id+"F8.boolean.opBoolean","INTERSECT",EDGE,{"derivedFrom":[makeQuery(id+"F5.boolean.opBoolean","SPLIT",FACE,{"disambiguationData":[TD([makeQuery(id+"F2.opExtrude","SWEPT_FACE",FACE,{"disambiguationData":[OSD([subQ5])]})])],"derivedFrom":makeQuery(id+"F3.boolean.opBoolean","COPY",FACE,{"derivedFrom":makeQuery(id+"F3.opExtrude","CAP_FACE",FACE,{"disambiguationData":[OSD([subQ5,subQ1,subQ6,subQ7,subQ4,subQ3,subQ2,subQ0])],"isStart":false})})}),makeQuery(id+"F8.opExtrude","SWEPT_FACE",FACE,{"disambiguationData":[OSD([sQuery(id+"F7.wireOp",EDGE,"E67")])]})]});}
            var Q5;
            Q5=makeQuery(id+"F8.boolean.opBoolean","INTERSECT",EDGE,{"disambiguationData":[OD(0.0)],"derivedFrom":[makeQuery(id+"F5.opExtrude","SWEPT_FACE",FACE,{"disambiguationData":[OSD([sQuery(id+"F4.wireOp",EDGE,"E30")])]}),makeQuery(id+"F8.opExtrude","SWEPT_FACE",FACE,{"disambiguationData":[OSD([sQuery(id+"F7.wireOp",EDGE,"E67")])]})]});
            fillet(context, id + "F14", {"entities" : qUnion([Q0, Q1, Q2, Q3, Q4, Q5]), "radius" : 3 * mm, "tangentPropagation" : true, "allowEdgeOverflow" : false});
        }
        {
            var Q0;
            Q0=makeQuery(id+"F1.opExtrude","CAP_EDGE",EDGE,{"disambiguationData":[OSD([sQuery(id+"F0.wireOp",EDGE,"E1.bottom")])],"isStart":false});
            fillet(context, id + "F15", {"entities" : qUnion([Q0]), "radius" : 2 * mm, "tangentPropagation" : true, "allowEdgeOverflow" : false});
        }
        {
            var Q0;
            {var subQ0=sQuery(id+"F0.wireOp",EDGE,"E21.filletArc");var subQ1=sQuery(id+"F0.wireOp",EDGE,"E7");var subQ2=sQuery(id+"F0.wireOp",EDGE,"E6");var subQ3=sQuery(id+"F0.wireOp",EDGE,"E5");var subQ4=sQuery(id+"F0.wireOp",EDGE,"E4");var subQ5=sQuery(id+"F0.wireOp",EDGE,"E22.filletArc");var subQ6=sQuery(id+"F0.wireOp",EDGE,"E1.bottom");var subQ7=sQuery(id+"F0.wireOp",EDGE,"E1.right");var subQ8=sQuery(id+"F0.wireOp",EDGE,"E1.top");var subQ9=sQuery(id+"F0.wireOp",EDGE,"E1.left");var subQ10=sQuery(id+"F0.wireOp",EDGE,"E23.filletArc");var subQ11=sQuery(id+"F0.wireOp",EDGE,"E24.filletArc");Q0=makeQuery(id+"F2.boolean.opBoolean","SPLIT",FACE,{"disambiguationData":[TD([makeQuery(id+"F1.opExtrude","SWEPT_FACE",FACE,{"disambiguationData":[OSD([subQ6])]})])],"derivedFrom":makeQuery(id+"F1.opExtrude","CAP_FACE",FACE,{"disambiguationData":[OSD([subQ6,subQ8,subQ9,subQ7,subQ4,subQ3,subQ2,subQ1,subQ0,subQ5,subQ10,subQ11])],"isStart":true})});}
            var sketch = newSketch(context, id + "F16", { "sketchPlane" : qUnion([Q0])});
            skLineSegment(sketch, "E79", {"start": v(-33, 80) * mm, "end": v(-15, 98) * mm});
            skLineSegment(sketch, "E80", {"start": v(-15, 98) * mm, "end": v(-15, 110) * mm});
            skArc(sketch, "E81", {"start": v(15, 110) * mm, "mid": v(0, 125) * mm, "end": v(-15, 110) * mm});
            skLineSegment(sketch, "E82", {"start": v(15, 110) * mm, "end": v(15, 98) * mm});
            skLineSegment(sketch, "E83", {"start": v(15, 98) * mm, "end": v(33, 80) * mm});
            skCircle(sketch, "E84", {"center": v(0, 110) * mm, "radius": 6 * mm});
            skLineSegment(sketch, "E85", {"start": v(0, 110) * mm, "end": v(0, 80) * mm, "construction": true});
            skLineSegment(sketch, "E86", {"start": v(-80, 0) * mm, "end": v(80, 0) * mm, "construction": true});
            skArc(sketch, "E87.MirrorCS", {"start": v(15, -110) * mm, "mid": v(0, -125) * mm, "end": v(-15, -110) * mm});
            skCircle(sketch, "E88.MirrorC", {"center": v(0, -110) * mm, "radius": 6 * mm});
            skLineSegment(sketch, "E89.MirrorCS", {"start": v(15, -110) * mm, "end": v(15, -98) * mm});
            skLineSegment(sketch, "E90.MirrorCS", {"start": v(-15, -98) * mm, "end": v(-15, -110) * mm});
            skLineSegment(sketch, "E91.MirrorCS", {"start": v(-33, -80) * mm, "end": v(-15, -98) * mm});
            skLineSegment(sketch, "E92.MirrorCS", {"start": v(15, -98) * mm, "end": v(33, -80) * mm});
            skLineSegment(sketch, "E93.MirrorCS", {"start": v(0, -110) * mm, "end": v(0, -80) * mm, "construction": true});
            skSolve(sketch);
        }
        {
            var Q0;
            {var subQ0=sQuery(id+"F16.wireOp",EDGE,"E79");Q0=makeQuery(id+"F16.imprint","IMPRINT",FACE,{"disambiguationData":[TD([[makeQuery(id+"F16.imprint","IMPRINT",EDGE,{"derivedFrom":subQ0}),-1.0]])]});}
            var Q1;
            Q1=makeQuery(id+"F16.imprint","IMPRINT",FACE,{"disambiguationData":[TD([[makeQuery(id+"F16.imprint","IMPRINT",EDGE,{"derivedFrom":makeQuery(id+"F1.opExtrude","CAP_EDGE",EDGE,{"disambiguationData":[OSD([sQuery(id+"F0.wireOp",EDGE,"E1.left")])],"isStart":true})}),-1.0]])]});
            var Q2;
            Q2=makeQuery(id+"F16.imprint","IMPRINT",FACE,{"disambiguationData":[TD([[makeQuery(id+"F16.imprint","IMPRINT",EDGE,{"derivedFrom":sQuery(id+"F16.wireOp",EDGE,"E87.MirrorCS")}),-1.0]])]});
            var Q3;
            Q3=makeQuery(id+"F2.opExtrude","CAP_FACE",FACE,{"disambiguationData":[OSD([sQuery(id+"F0.wireOp",EDGE,"E12"),sQuery(id+"F0.wireOp",EDGE,"E13"),sQuery(id+"F0.wireOp",EDGE,"E14"),sQuery(id+"F0.wireOp",EDGE,"E15"),sQuery(id+"F0.wireOp",EDGE,"E17.filletArc"),sQuery(id+"F0.wireOp",EDGE,"E18.filletArc"),sQuery(id+"F0.wireOp",EDGE,"E19.filletArc"),sQuery(id+"F0.wireOp",EDGE,"E20.filletArc"),sQuery(id+"F0.wireOp",EDGE,"E25.0"),sQuery(id+"F0.wireOp",EDGE,"E25.1"),sQuery(id+"F0.wireOp",EDGE,"E25.2"),sQuery(id+"F0.wireOp",EDGE,"E25.3"),sQuery(id+"F0.wireOp",EDGE,"E25.4"),sQuery(id+"F0.wireOp",EDGE,"E25.5"),sQuery(id+"F0.wireOp",EDGE,"E25.6"),sQuery(id+"F0.wireOp",EDGE,"E25.7")])],"isStart":false});
            extrude(context, id + "F17", {"entities" : qUnion([Q0, Q1, Q2]), "endBound" : BoundingType.UP_TO_SURFACE, "endBoundEntityFace" : qUnion([Q3]), "depth" : 25 * mm});
        }
    });
